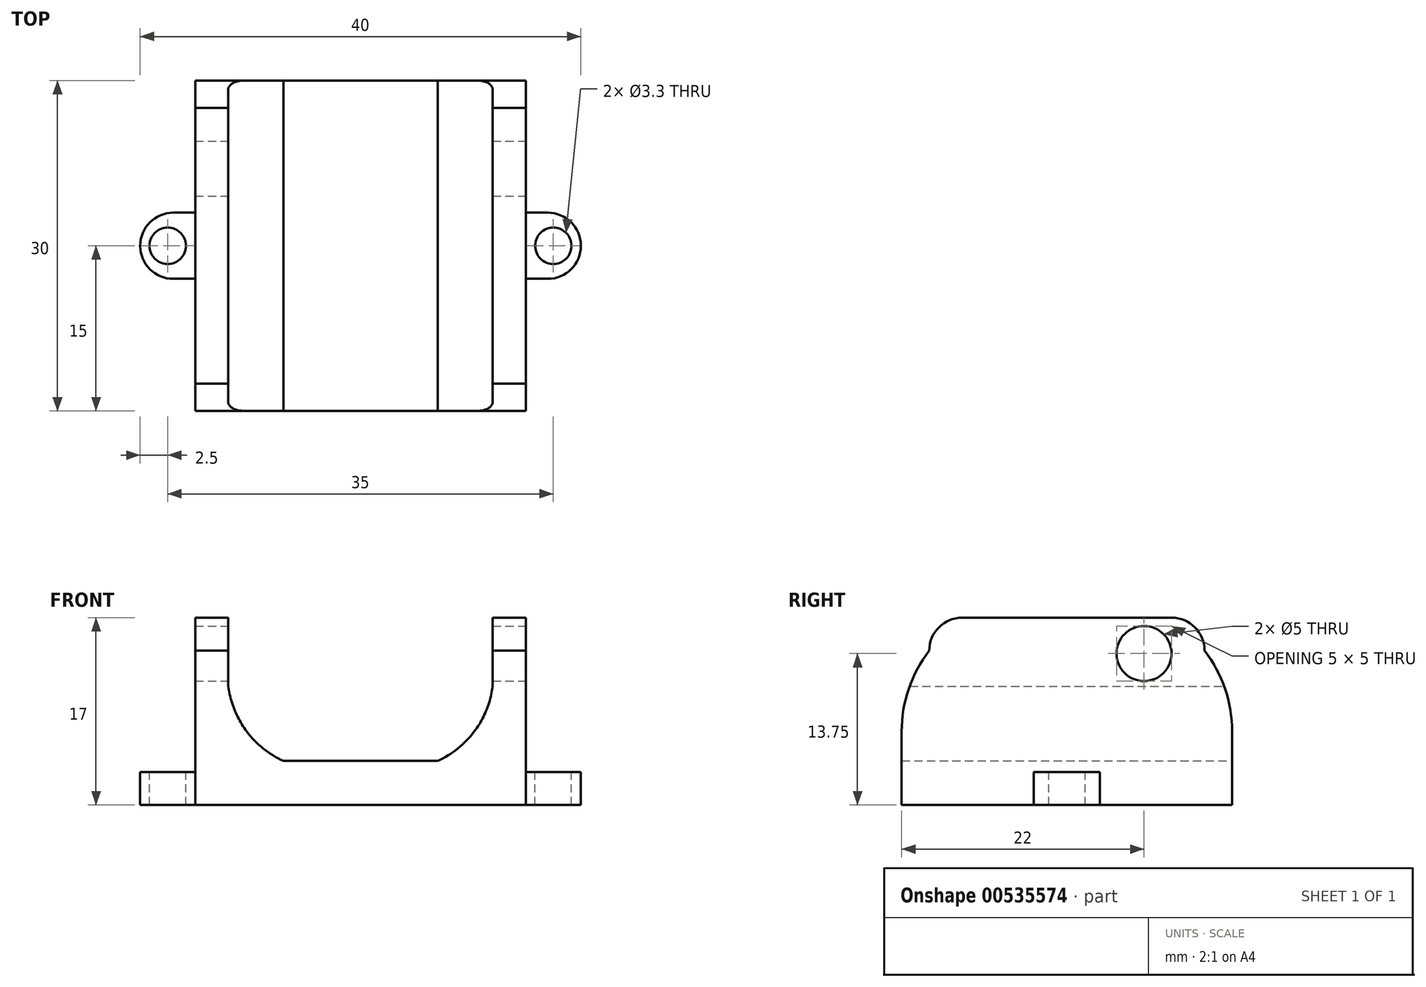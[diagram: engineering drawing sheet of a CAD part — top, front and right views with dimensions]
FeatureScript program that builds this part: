
annotation { "Feature Type Name" : "Feature", "Feature Type Description" : "" }
export const myFeature = defineFeature(function(context is Context, id is Id, definition is map)
    precondition{}
    {
        {
            var Q0;
            Q0=qCreatedBy(makeId("Top.planeOp"),FACE);
            var sketch = newSketch(context, id + "F0", { "sketchPlane" : qUnion([Q0])});
            skLineSegment(sketch, "E0.bottom", {"start": v(-15, -15) * mm, "end": v(15, -15) * mm});
            skLineSegment(sketch, "E0.top", {"start": v(-15, 15) * mm, "end": v(15, 15) * mm});
            skLineSegment(sketch, "E0.left", {"start": v(-15, -15) * mm, "end": v(-15, 15) * mm});
            skLineSegment(sketch, "E0.right", {"start": v(15, -15) * mm, "end": v(15, 15) * mm});
            skPoint(sketch, "E0.middle", {"position": v(0, 0) * mm});
            skSolve(sketch);
        }
        {
            var Q0;
            Q0 = qSketchRegion(id + "F0", true);
            extrude(context, id + "F1", {"entities" : qUnion([Q0]), "oppositeDirection" : true, "depth" : 4 * mm, "offsetDistance" : 25 * mm});
        }
        {
            var Q0;
            Q0=qCreatedBy(makeId("Front.planeOp"),FACE);
            var sketch = newSketch(context, id + "F2", { "sketchPlane" : qUnion([Q0])});
            skLineSegment(sketch, "E1.bottom", {"start": v(-15, 0) * mm, "end": v(-12, 0) * mm});
            skLineSegment(sketch, "E1.top", {"start": v(-15, 10) * mm, "end": v(-12, 10) * mm});
            skLineSegment(sketch, "E1.left", {"start": v(-15, 0) * mm, "end": v(-15, 10) * mm});
            skLineSegment(sketch, "E1.right", {"start": v(-12, 0) * mm, "end": v(-12, 10) * mm});
            skLineSegment(sketch, "E2.bottom", {"start": v(15, 0) * mm, "end": v(12, 0) * mm});
            skLineSegment(sketch, "E2.top", {"start": v(15, 10) * mm, "end": v(12, 10) * mm});
            skLineSegment(sketch, "E2.left", {"start": v(15, 0) * mm, "end": v(15, 10) * mm});
            skLineSegment(sketch, "E2.right", {"start": v(12, 0) * mm, "end": v(12, 10) * mm});
            skSolve(sketch);
        }
        {
            var Q0;
            Q0 = qSketchRegion(id + "F2", true);
            extrude(context, id + "F3", {"entities" : qUnion([Q0]), "operationType" : NewBodyOperationType.ADD, "depth" : 30 * mm, "offsetDistance" : 25 * mm, "symmetric" : true});
        }
        {
            var Q0;
            Q0=qCreatedBy(makeId("Front.planeOp"),FACE);
            var sketch = newSketch(context, id + "F4", { "sketchPlane" : qUnion([Q0])});
            skArc(sketch, "E3", {"start": v(-12, 9) * mm, "mid": v(-10.98, 3.68) * mm, "end": v(-7, 0) * mm});
            skLineSegment(sketch, "E4", {"start": v(-7, 0) * mm, "end": v(-12, 0) * mm});
            skLineSegment(sketch, "E5", {"start": v(-12, 0) * mm, "end": v(-12, 9) * mm});
            skArc(sketch, "E6.MirrorCS", {"start": v(12, 9) * mm, "mid": v(10.98, 3.68) * mm, "end": v(7, 0) * mm});
            skLineSegment(sketch, "E7.MirrorCS", {"start": v(7, 0) * mm, "end": v(12, 0) * mm});
            skLineSegment(sketch, "E8.MirrorCS", {"start": v(12, 0) * mm, "end": v(12, 9) * mm});
            skSolve(sketch);
        }
        {
            var Q0;
            Q0 = qSketchRegion(id + "F4", true);
            extrude(context, id + "F5", {"entities" : qUnion([Q0]), "operationType" : NewBodyOperationType.ADD, "depth" : 30 * mm, "offsetDistance" : 25 * mm, "symmetric" : true});
        }
        {
            var Q0;
            Q0=qCreatedBy(makeId("Front.planeOp"),FACE);
            var sketch = newSketch(context, id + "F6", { "sketchPlane" : qUnion([Q0])});
            skLineSegment(sketch, "E9.bottom", {"start": v(-15, -4) * mm, "end": v(-20, -4) * mm});
            skLineSegment(sketch, "E9.top", {"start": v(-15, -1) * mm, "end": v(-20, -1) * mm});
            skLineSegment(sketch, "E9.left", {"start": v(-15, -4) * mm, "end": v(-15, -1) * mm});
            skLineSegment(sketch, "E9.right", {"start": v(-20, -4) * mm, "end": v(-20, -1) * mm});
            skLineSegment(sketch, "E10.MirrorCS", {"start": v(15, -1) * mm, "end": v(20, -1) * mm});
            skLineSegment(sketch, "E11.MirrorCS", {"start": v(20, -4) * mm, "end": v(20, -1) * mm});
            skLineSegment(sketch, "E12.MirrorCS", {"start": v(15, -4) * mm, "end": v(20, -4) * mm});
            skLineSegment(sketch, "E13.MirrorCS", {"start": v(15, -4) * mm, "end": v(15, -1) * mm});
            skSolve(sketch);
        }
        {
            var Q0;
            Q0 = qSketchRegion(id + "F6", true);
            extrude(context, id + "F7", {"entities" : qUnion([Q0]), "operationType" : NewBodyOperationType.ADD, "depth" : 6 * mm, "offsetDistance" : 25 * mm, "symmetric" : true});
        }
        {
            var Q0;
            Q0=makeQuery(id+"F7.opExtrude","CAP_EDGE",EDGE,{"disambiguationData":[OSD([sQuery(id+"F6.wireOp",EDGE,"E9.right")])],"isStart":true});
            var Q1;
            Q1=makeQuery(id+"F7.opExtrude","CAP_EDGE",EDGE,{"disambiguationData":[OSD([sQuery(id+"F6.wireOp",EDGE,"E9.right")])],"isStart":false});
            var Q2;
            Q2=makeQuery(id+"F7.opExtrude","CAP_EDGE",EDGE,{"disambiguationData":[OSD([sQuery(id+"F6.wireOp",EDGE,"E11.MirrorCS")])],"isStart":true});
            var Q3;
            Q3=makeQuery(id+"F7.opExtrude","CAP_EDGE",EDGE,{"disambiguationData":[OSD([sQuery(id+"F6.wireOp",EDGE,"E11.MirrorCS")])],"isStart":false});
            fillet(context, id + "F8", {"entities" : qUnion([Q0, Q1, Q2, Q3]), "radius" : 3 * mm, "tangentPropagation" : true, "allowEdgeOverflow" : false});
        }
        {
            var Q0;
            Q0=qCreatedBy(makeId("Top.planeOp"),FACE);
            var sketch = newSketch(context, id + "F9", { "sketchPlane" : qUnion([Q0])});
            skCircle(sketch, "E14", {"center": v(-17.5, 0) * mm, "radius": 1.65 * mm});
            skCircle(sketch, "E15.MirrorC", {"center": v(17.5, 0) * mm, "radius": 1.65 * mm});
            skSolve(sketch);
        }
        {
            var Q0;
            Q0 = qSketchRegion(id + "F9", true);
            extrude(context, id + "F10", {"entities" : qUnion([Q0]), "operationType" : NewBodyOperationType.REMOVE, "oppositeDirection" : true, "depth" : 25 * mm, "offsetDistance" : 25 * mm});
        }
        {
            var Q0;
            Q0=qCreatedBy(makeId("Front.planeOp"),FACE);
            var sketch = newSketch(context, id + "F11", { "sketchPlane" : qUnion([Q0])});
            skLineSegment(sketch, "E16.bottom", {"start": v(-15, 10) * mm, "end": v(-12, 10) * mm});
            skLineSegment(sketch, "E16.top", {"start": v(-15, 13) * mm, "end": v(-12, 13) * mm});
            skLineSegment(sketch, "E16.left", {"start": v(-15, 10) * mm, "end": v(-15, 13) * mm});
            skLineSegment(sketch, "E16.right", {"start": v(-12, 10) * mm, "end": v(-12, 13) * mm});
            skLineSegment(sketch, "E17.MirrorCS", {"start": v(12, 10) * mm, "end": v(12, 13) * mm});
            skLineSegment(sketch, "E18.MirrorCS", {"start": v(15, 13) * mm, "end": v(12, 13) * mm});
            skLineSegment(sketch, "E19.MirrorCS", {"start": v(15, 10) * mm, "end": v(15, 13) * mm});
            skLineSegment(sketch, "E20.MirrorCS", {"start": v(15, 10) * mm, "end": v(12, 10) * mm});
            skSolve(sketch);
        }
        {
            var Q0;
            Q0 = qSketchRegion(id + "F11", true);
            extrude(context, id + "F12", {"entities" : qUnion([Q0]), "operationType" : NewBodyOperationType.ADD, "depth" : 25 * mm, "offsetDistance" : 25 * mm, "symmetric" : true});
        }
        {
            var Q0;
            Q0=makeQuery(id+"F12.opExtrude","CAP_EDGE",EDGE,{"disambiguationData":[OSD([sQuery(id+"F11.wireOp",EDGE,"E16.top")])],"isStart":false});
            var Q1;
            Q1=makeQuery(id+"F12.opExtrude","CAP_EDGE",EDGE,{"disambiguationData":[OSD([sQuery(id+"F11.wireOp",EDGE,"E16.top")])],"isStart":true});
            var Q2;
            Q2=makeQuery(id+"F12.opExtrude","CAP_EDGE",EDGE,{"disambiguationData":[OSD([sQuery(id+"F11.wireOp",EDGE,"E18.MirrorCS")])],"isStart":false});
            var Q3;
            Q3=makeQuery(id+"F12.opExtrude","CAP_EDGE",EDGE,{"disambiguationData":[OSD([sQuery(id+"F11.wireOp",EDGE,"E18.MirrorCS")])],"isStart":true});
            fillet(context, id + "F13", {"entities" : qUnion([Q0, Q1, Q2, Q3]), "radius" : 3 * mm, "tangentPropagation" : true, "allowEdgeOverflow" : false});
        }
        {
            var Q0;
            Q0=qCreatedBy(makeId("Right.planeOp"),FACE);
            var sketch = newSketch(context, id + "F14", { "sketchPlane" : qUnion([Q0])});
            skPoint(sketch, "E21.visualSharp", {"position": v(7, 12.5) * mm});
            skCircle(sketch, "E22", {"center": v(7, 9.75) * mm, "radius": 2.5 * mm});
            skSolve(sketch);
        }
        {
            var Q0;
            Q0 = qSketchRegion(id + "F14", true);
            extrude(context, id + "F15", {"entities" : qUnion([Q0]), "operationType" : NewBodyOperationType.REMOVE, "oppositeDirection" : true, "depth" : 37.6 * mm, "offsetDistance" : 25 * mm, "symmetric" : true});
        }
        {
            var Q0;
            Q0=makeQuery(id+"F3.opExtrude","CAP_EDGE",EDGE,{"disambiguationData":[OSD([sQuery(id+"F2.wireOp",EDGE,"E2.top")])],"isStart":true});
            var Q1;
            Q1=makeQuery(id+"F3.opExtrude","CAP_EDGE",EDGE,{"disambiguationData":[OSD([sQuery(id+"F2.wireOp",EDGE,"E2.top")])],"isStart":false});
            var Q2;
            Q2=makeQuery(id+"F3.opExtrude","CAP_EDGE",EDGE,{"disambiguationData":[OSD([sQuery(id+"F2.wireOp",EDGE,"E1.top")])],"isStart":false});
            var Q3;
            Q3=makeQuery(id+"F3.opExtrude","CAP_EDGE",EDGE,{"disambiguationData":[OSD([sQuery(id+"F2.wireOp",EDGE,"E1.top")])],"isStart":true});
            fillet(context, id + "F16", {"entities" : qUnion([Q0, Q1, Q2, Q3]), "radius" : 12 * mm, "tangentPropagation" : true, "allowEdgeOverflow" : false});
        }
    });
